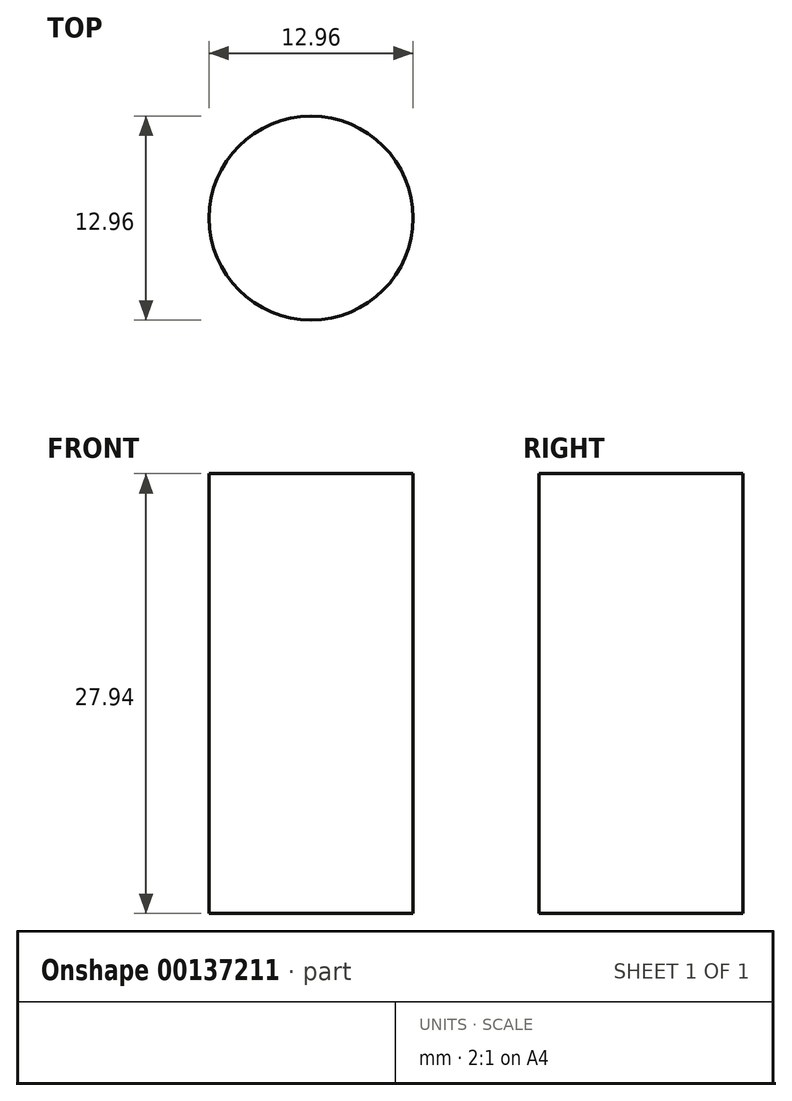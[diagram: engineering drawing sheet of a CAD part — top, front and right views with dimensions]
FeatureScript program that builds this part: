
annotation { "Feature Type Name" : "Feature", "Feature Type Description" : "" }
export const myFeature = defineFeature(function(context is Context, id is Id, definition is map)
    precondition{}
    {
        {
            var Q0;
            Q0=qCreatedBy(makeId("Top.planeOp"), FACE);
            var sketch = newSketch(context, id + "F0", { "sketchPlane" : qUnion([Q0])});
            skCircle(sketch, "E0", {"center": v(0, 0) * mm, "radius": 6.48 * mm});
            skSolve(sketch);
        }
        {
            var Q0;
            Q0 = qSketchRegion(id + "F0", true);
            extrude(context, id + "F1", {"entities" : qUnion([Q0]), "depth" : 27.94 * mm, "offsetDistance" : 25.4 * mm});
        }
    });
